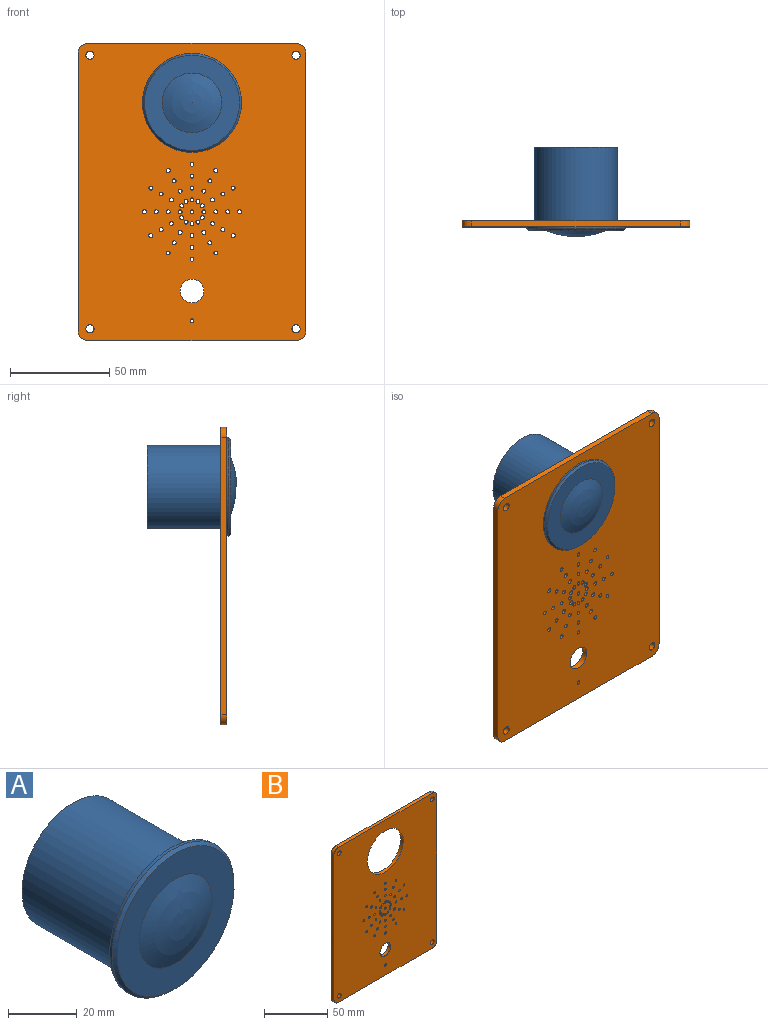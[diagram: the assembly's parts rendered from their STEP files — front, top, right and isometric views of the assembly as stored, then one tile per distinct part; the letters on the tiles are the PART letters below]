
ASSEMBLY  parts=2 mates=1
PART A: 7 faces, bbox 50x44.9x50 mm
  f0: plane 42x42mm, normal (0,1,0), area 1385.4mm2, adj f1
  f1: cylinder r=21mm len=42mm, axis (0,1,0), area 5277.9mm2, adj f0,f2
  f2: plane 50x50mm, normal (0,1,0), area 578.1mm2, adj f1,f3
  f3: cylinder r=25mm len=50mm, axis (0,1,0), area 157.1mm2, adj f2,f6
  f4: plane 48x48mm, normal (0,-1,0), area 1102.7mm2, adj f5,f6
  f5: sphere r=40mm, area 733.6mm2, adj f4
  f6: cone r=25mm half-angle=45deg, axis (0,1,0), area 217.7mm2, adj f3,f4
PART B: 66 faces, bbox 115x3x150 mm
  f0: plane 140x3mm, normal (1,0,0), area 420mm2, adj f4,f5,f58,f61
  f1: plane 105x3mm, normal (0,0,1), area 315mm2, adj f4,f5,f58,f59
  f2: plane 140x3mm, normal (-1,0,0), area 420mm2, adj f4,f5,f59,f60
  f3: plane 105x3mm, normal (0,0,-1), area 315mm2, adj f4,f5,f60,f61
  f4: plane 150x115mm, normal (0,-1,0), area 15648.3mm2, adj f0,f1,f2,f3,f6,f7,f8,f9
  f5: plane 150x115mm, normal (0,1,0), area 15648.3mm2, adj f0,f1,f2,f3,f6,f7,f8,f9
  f6: cylinder r=20mm len=40mm, axis (0,-1,0), area 377mm2, adj f4,f5
  f7: cylinder r=1mm len=3mm, axis (0,-1,0), area 18.8mm2, adj f4,f5
  f8: cylinder r=1mm len=3mm, axis (0,-1,0), area 18.8mm2, adj f4,f5
  f9: cylinder r=1mm len=3mm, axis (0,-1,0), area 18.8mm2, adj f4,f5
  f10: cylinder r=1mm len=3mm, axis (0,-1,0), area 18.8mm2, adj f4,f5
  f11: cylinder r=1mm len=3mm, axis (0,-1,0), area 18.8mm2, adj f4,f5
  f12: cylinder r=1mm len=3mm, axis (0,-1,0), area 18.8mm2, adj f4,f5
  f13: cylinder r=1mm len=3mm, axis (0,-1,0), area 18.8mm2, adj f4,f5
  f14: cylinder r=1mm len=3mm, axis (0,-1,0), area 18.8mm2, adj f4,f5
  f15: cylinder r=1mm len=3mm, axis (0,-1,0), area 18.8mm2, adj f4,f5
  f16: cylinder r=1mm len=3mm, axis (0,-1,0), area 18.8mm2, adj f4,f5
  f17: cylinder r=1mm len=3mm, axis (0,-1,0), area 18.8mm2, adj f4,f5
  f18: cylinder r=1mm len=3mm, axis (0,-1,0), area 18.8mm2, adj f4,f5
  f19: cylinder r=1mm len=3mm, axis (0,-1,0), area 18.8mm2, adj f4,f5
  f20: cylinder r=1mm len=3mm, axis (0,-1,0), area 18.8mm2, adj f4,f5
  f21: cylinder r=1mm len=3mm, axis (0,-1,0), area 18.8mm2, adj f4,f5
  f22: cylinder r=1mm len=3mm, axis (0,-1,0), area 18.8mm2, adj f4,f5
  f23: cylinder r=1mm len=3mm, axis (0,-1,0), area 18.8mm2, adj f4,f5
  f24: cylinder r=1mm len=3mm, axis (0,-1,0), area 18.8mm2, adj f4,f5
  f25: cylinder r=1mm len=3mm, axis (0,-1,0), area 18.8mm2, adj f4,f5
  f26: cylinder r=1mm len=3mm, axis (0,-1,0), area 18.8mm2, adj f4,f5
  f27: cylinder r=1mm len=3mm, axis (0,-1,0), area 18.8mm2, adj f4,f5
  f28: cylinder r=1mm len=3mm, axis (0,-1,0), area 18.8mm2, adj f4,f5
  f29: cylinder r=1mm len=3mm, axis (0,-1,0), area 18.8mm2, adj f4,f5
  f30: cylinder r=1mm len=3mm, axis (0,-1,0), area 18.8mm2, adj f4,f5
  f31: cylinder r=1mm len=3mm, axis (0,-1,0), area 18.8mm2, adj f4,f5
  f32: cylinder r=1mm len=3mm, axis (0,-1,0), area 18.8mm2, adj f4,f5
  f33: cylinder r=1mm len=3mm, axis (0,-1,0), area 18.8mm2, adj f4,f5
  f34: cylinder r=1mm len=3mm, axis (0,-1,0), area 18.8mm2, adj f4,f5
  f35: cylinder r=1mm len=3mm, axis (0,-1,0), area 18.8mm2, adj f4,f5
  f36: cylinder r=1mm len=3mm, axis (0,-1,0), area 18.8mm2, adj f4,f5
  f37: cylinder r=1mm len=3mm, axis (0,-1,0), area 18.8mm2, adj f4,f5
  f38: cylinder r=1mm len=3mm, axis (0,-1,0), area 18.8mm2, adj f4,f5
  f39: cylinder r=1mm len=3mm, axis (0,-1,0), area 18.8mm2, adj f4,f5
  f40: cylinder r=1mm len=3mm, axis (0,-1,0), area 18.8mm2, adj f4,f5
  f41: cylinder r=1mm len=3mm, axis (0,-1,0), area 18.8mm2, adj f4,f5
  f42: cylinder r=1mm len=3mm, axis (0,-1,0), area 18.8mm2, adj f4,f5
  f43: cylinder r=1mm len=3mm, axis (0,-1,0), area 18.8mm2, adj f4,f5
  f44: cylinder r=1mm len=3mm, axis (0,-1,0), area 18.8mm2, adj f4,f5
  f45: cylinder r=1mm len=3mm, axis (0,-1,0), area 18.8mm2, adj f4,f5
  f46: cylinder r=1mm len=3mm, axis (0,-1,0), area 18.8mm2, adj f4,f5
  f47: cylinder r=1mm len=3mm, axis (0,-1,0), area 18.8mm2, adj f4,f5
  f48: cylinder r=1mm len=3mm, axis (0,-1,0), area 18.8mm2, adj f4,f5
  f49: cylinder r=1mm len=3mm, axis (0,-1,0), area 18.8mm2, adj f4,f5
  f50: cylinder r=1mm len=3mm, axis (0,-1,0), area 18.8mm2, adj f4,f5
  f51: cylinder r=1mm len=3mm, axis (0,-1,0), area 18.8mm2, adj f4,f5
  f52: cylinder r=1mm len=3mm, axis (0,-1,0), area 18.8mm2, adj f4,f5
  f53: cylinder r=1mm len=3mm, axis (0,-1,0), area 18.8mm2, adj f4,f5
  f54: cylinder r=1mm len=3mm, axis (0,-1,0), area 18.8mm2, adj f4,f5
  f55: cylinder r=1mm len=3mm, axis (0,-1,0), area 18.8mm2, adj f4,f5
  f56: cylinder r=6mm len=12mm, axis (0,-1,0), area 113.1mm2, adj f4,f5
  f57: cylinder r=1mm len=3mm, axis (0,-1,0), area 18.8mm2, adj f4,f5
  f58: cylinder r=5mm len=5mm, axis (0,-1,0), area 23.6mm2, adj f0,f1,f4,f5
  f59: cylinder r=5mm len=5mm, axis (0,1,0), area 23.6mm2, adj f1,f2,f4,f5
  f60: cylinder r=5mm len=5mm, axis (0,-1,0), area 23.6mm2, adj f2,f3,f4,f5
  f61: cylinder r=5mm len=5mm, axis (0,1,0), area 23.6mm2, adj f0,f3,f4,f5
  f62: cylinder r=2.06mm len=4.12mm, axis (0,-1,0), area 38.9mm2, adj f4,f5
  f63: cylinder r=2.06mm len=4.12mm, axis (0,-1,0), area 38.9mm2, adj f4,f5
  f64: cylinder r=2.06mm len=4.12mm, axis (0,-1,0), area 38.9mm2, adj f4,f5
  f65: cylinder r=2.06mm len=4.12mm, axis (0,-1,0), area 38.9mm2, adj f4,f5
PLACE A t=(-121.49,-79.88,42.29)mm
PLACE B t=(-121.49,-91.52,-12.71)mm
MATE cylindrical A.f1 <-> B.f6  axis (0,1,0) through (-121.49,-94.52,42.29)mm
